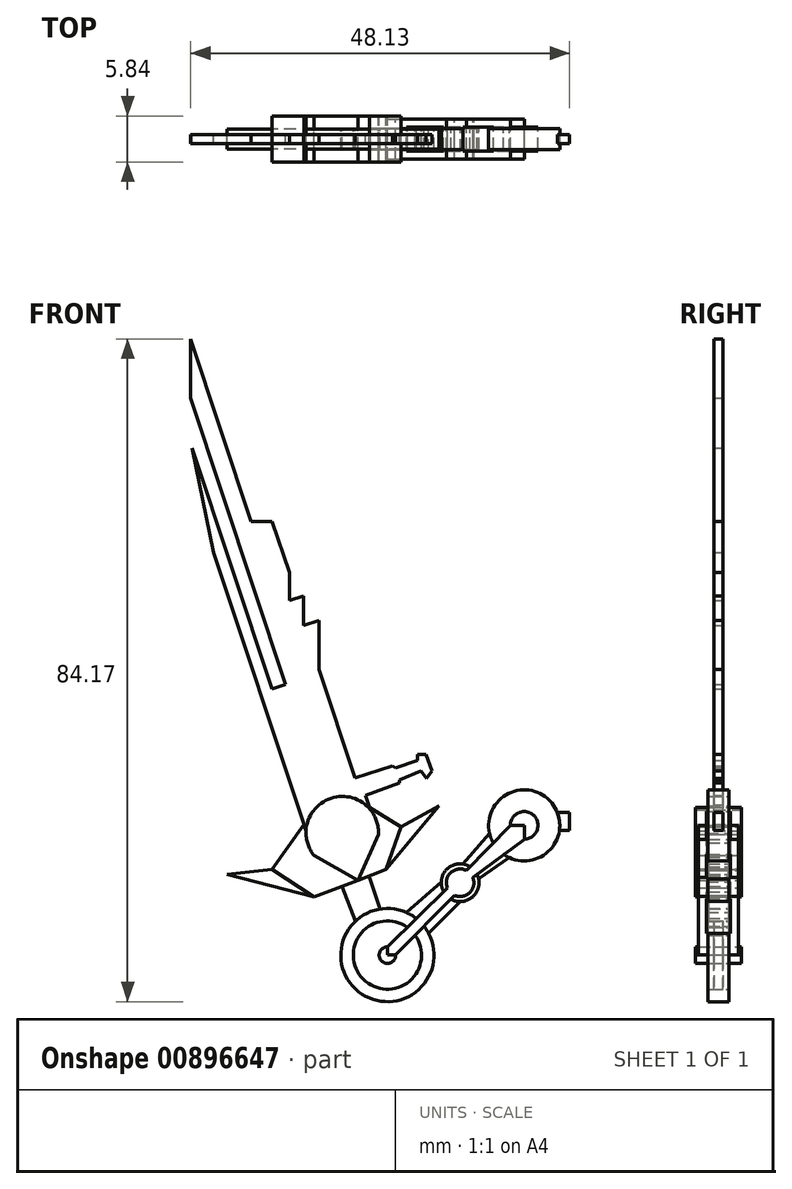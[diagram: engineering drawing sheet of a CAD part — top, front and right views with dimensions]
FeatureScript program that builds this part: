
annotation { "Feature Type Name" : "Feature", "Feature Type Description" : "" }
export const myFeature = defineFeature(function(context is Context, id is Id, definition is map)
    precondition{}
    {
        {
            var Q0;
            Q0=qCreatedBy(makeId("Front.planeOp"),FACE);
            var sketch = newSketch(context, id + "F0", { "sketchPlane" : qUnion([Q0])});
            skLineSegment(sketch, "E0.bottom", {"start": v(-15.76, 7.28) * mm, "end": v(19.82, 7.28) * mm});
            skLineSegment(sketch, "E0.left", {"start": v(-15.76, 7.28) * mm, "end": v(-15.76, 1.57) * mm});
            skLineSegment(sketch, "E0.right", {"start": v(19.82, 7.28) * mm, "end": v(19.82, 1.57) * mm});
            skLineSegment(sketch, "E1", {"start": v(-15.76, 7.28) * mm, "end": v(-19.45, 11.89) * mm});
            skLineSegment(sketch, "E2", {"start": v(23.14, 11.89) * mm, "end": v(19.82, 7.28) * mm});
            skArc(sketch, "E3", {"start": v(23.14, 11.89) * mm, "mid": v(1.84, 40) * mm, "end": v(-19.45, 11.89) * mm});
            skLineSegment(sketch, "E4", {"start": v(-5.9, 38.59) * mm, "end": v(-5.9, 55.58) * mm});
            skLineSegment(sketch, "E5", {"start": v(-5.9, 55.58) * mm, "end": v(-13.15, 34.14) * mm});
            skLineSegment(sketch, "E6", {"start": v(6.13, 39.57) * mm, "end": v(6.13, 56.13) * mm});
            skLineSegment(sketch, "E7", {"start": v(6.13, 56.13) * mm, "end": v(13.75, 36.51) * mm});
            skLineSegment(sketch, "E8", {"start": v(-39.06, 0) * mm, "end": v(-48.21, -3.47) * mm});
            skLineSegment(sketch, "E9", {"start": v(-48.21, -3.47) * mm, "end": v(-53.56, 0) * mm});
            skLineSegment(sketch, "E10", {"start": v(-37.15, 5.44) * mm, "end": v(-39.06, 0) * mm});
            skLineSegment(sketch, "E11", {"start": v(-48.21, 1.77) * mm, "end": v(-60.97, 40.27) * mm});
            skLineSegment(sketch, "E12", {"start": v(-60.97, 40.27) * mm, "end": v(-63.7, 53.56) * mm});
            skLineSegment(sketch, "E13", {"start": v(-63.7, 53.56) * mm, "end": v(-53.56, 22.96) * mm});
            skLineSegment(sketch, "E14", {"start": v(-53.56, 22.96) * mm, "end": v(-51.84, 23.53) * mm});
            skLineSegment(sketch, "E15", {"start": v(-51.84, 23.53) * mm, "end": v(-63.9, 59.88) * mm});
            skLineSegment(sketch, "E16", {"start": v(-63.9, 59.88) * mm, "end": v(-63.9, 67.38) * mm});
            skLineSegment(sketch, "E17", {"start": v(-63.9, 67.38) * mm, "end": v(-57.09, 46.85) * mm});
            skLineSegment(sketch, "E18", {"start": v(-57.09, 46.85) * mm, "end": v(-56.2, 44.2) * mm});
            skLineSegment(sketch, "E19", {"start": v(-56.2, 44.2) * mm, "end": v(-53.56, 44.2) * mm});
            skLineSegment(sketch, "E20", {"start": v(-40.03, 4.48) * mm, "end": v(-41.66, 9.4) * mm});
            skLineSegment(sketch, "E21", {"start": v(-38.25, 13.18) * mm, "end": v(-43.01, 11.6) * mm});
            skLineSegment(sketch, "E22", {"start": v(-43.01, 11.6) * mm, "end": v(-47.6, 25.43) * mm});
            skLineSegment(sketch, "E23", {"start": v(-47.6, 25.43) * mm, "end": v(-47.6, 31.62) * mm});
            skLineSegment(sketch, "E24", {"start": v(-47.6, 31.62) * mm, "end": v(-49.53, 30.98) * mm});
            skLineSegment(sketch, "E25", {"start": v(-49.53, 30.98) * mm, "end": v(-49.53, 34.75) * mm});
            skLineSegment(sketch, "E26", {"start": v(-49.53, 34.75) * mm, "end": v(-51.33, 34.15) * mm});
            skLineSegment(sketch, "E27", {"start": v(-51.33, 34.15) * mm, "end": v(-51.33, 37.7) * mm});
            skLineSegment(sketch, "E28", {"start": v(-51.33, 37.7) * mm, "end": v(-53.56, 44.2) * mm});
            skArc(sketch, "E29", {"start": v(-40.03, 4.48) * mm, "mid": v(-46.08, 9.06) * mm, "end": v(-48.21, 1.77) * mm});
            skLineSegment(sketch, "E30", {"start": v(-42.63, -1.36) * mm, "end": v(-40.03, 4.48) * mm});
            skLineSegment(sketch, "E31", {"start": v(-48.21, 1.77) * mm, "end": v(-42.63, -1.36) * mm});
            skLineSegment(sketch, "E32", {"start": v(-53.56, 0) * mm, "end": v(-49.52, 5.74) * mm});
            skLineSegment(sketch, "E33", {"start": v(-37.15, 5.44) * mm, "end": v(-41.66, 8.2) * mm});
            skArc(sketch, "E34", {"start": v(-10.97, 20.37) * mm, "mid": v(-7.92, 17.42) * mm, "end": v(-5.07, 20.56) * mm});
            skLineSegment(sketch, "E35", {"start": v(-10.97, 20.37) * mm, "end": v(-10.97, 28.85) * mm});
            skLineSegment(sketch, "E36", {"start": v(-5.07, 20.56) * mm, "end": v(-5.07, 28.48) * mm});
            skArc(sketch, "E37", {"start": v(-5.07, 28.48) * mm, "mid": v(-7.82, 31.8) * mm, "end": v(-10.97, 28.85) * mm});
            skArc(sketch, "E38", {"start": v(12.08, 28.85) * mm, "mid": v(9.4, 31.98) * mm, "end": v(6.73, 28.85) * mm});
            skLineSegment(sketch, "E39", {"start": v(6.73, 28.85) * mm, "end": v(6.73, 19.82) * mm});
            skLineSegment(sketch, "E40", {"start": v(12.08, 28.85) * mm, "end": v(12.08, 19.63) * mm});
            skArc(sketch, "E41", {"start": v(6.73, 19.82) * mm, "mid": v(9.31, 17.14) * mm, "end": v(12.08, 19.63) * mm});
            skLineSegment(sketch, "E42", {"start": v(-44.65, -2.12) * mm, "end": v(-42.94, -6.62) * mm});
            skLineSegment(sketch, "E43", {"start": v(-41.24, -0.83) * mm, "end": v(-39.86, -5.04) * mm});
            skCircle(sketch, "E44", {"center": v(-38.9, -10.87) * mm, "radius": 5.92 * mm});
            skCircle(sketch, "E45", {"center": v(-38.9, -10.87) * mm, "radius": 4.33 * mm});
            skCircle(sketch, "E46", {"center": v(-38.9, -10.87) * mm, "radius": 1.05 * mm});
            skFitSpline(sketch, "E47", {"points": [v(-15.76, 7.28) * mm, v(1.84, 17.87) * mm, v(19.82, 7.28) * mm], "startDerivative": vector(35.23, 31.82) * mm, "endDerivative": vector(35.93, -31.74) * mm});
            skCircle(sketch, "E48", {"center": v(-21.52, 5.6) * mm, "radius": 4.51 * mm});
            skLineSegment(sketch, "E49", {"start": v(-15.76, 7.28) * mm, "end": v(-17.33, 7.28) * mm});
            skLineSegment(sketch, "E50", {"start": v(-17.05, 4.97) * mm, "end": v(-15.76, 4.97) * mm});
            skCircle(sketch, "E51", {"center": v(-29.67, -1.68) * mm, "radius": 2.4 * mm});
            skLineSegment(sketch, "E52", {"start": v(-32.06, -1.6) * mm, "end": v(-36.48, -5.47) * mm});
            skLineSegment(sketch, "E53", {"start": v(-29.59, -4.07) * mm, "end": v(-33.65, -8.14) * mm});
            skLineSegment(sketch, "E54", {"start": v(-29.32, 0.7) * mm, "end": v(-25.92, 4.57) * mm});
            skLineSegment(sketch, "E55", {"start": v(-27.31, -1.22) * mm, "end": v(-23.42, 1.5) * mm});
            skCircle(sketch, "E56", {"center": v(-29.67, -1.68) * mm, "radius": 1.75 * mm});
            skCircle(sketch, "E57", {"center": v(-21.52, 5.6) * mm, "radius": 1.75 * mm});
            skLineSegment(sketch, "E58", {"start": v(-21.52, 5.6) * mm, "end": v(-23.27, 5.6) * mm});
            skLineSegment(sketch, "E59", {"start": v(-23.27, 5.6) * mm, "end": v(-28.85, -0.13) * mm});
            skLineSegment(sketch, "E60", {"start": v(-21.52, 5.6) * mm, "end": v(-21.52, 3.85) * mm});
            skLineSegment(sketch, "E61", {"start": v(-21.52, 3.85) * mm, "end": v(-28.06, -1) * mm});
            skLineSegment(sketch, "E62", {"start": v(-38.9, -10.87) * mm, "end": v(-38.9, -9.82) * mm});
            skLineSegment(sketch, "E63", {"start": v(-38.9, -9.82) * mm, "end": v(-31.28, -2.36) * mm});
            skLineSegment(sketch, "E64", {"start": v(-38.9, -10.87) * mm, "end": v(-37.85, -10.87) * mm});
            skLineSegment(sketch, "E65", {"start": v(-37.85, -10.87) * mm, "end": v(-30.38, -3.28) * mm});
            skLineSegment(sketch, "E66", {"start": v(-37.15, 5.44) * mm, "end": v(-32.36, 8.08) * mm});
            skLineSegment(sketch, "E67", {"start": v(-32.36, 8.08) * mm, "end": v(-39.06, 0) * mm});
            skLineSegment(sketch, "E68", {"start": v(-59.26, -0.64) * mm, "end": v(-48.21, -3.47) * mm});
            skLineSegment(sketch, "E69", {"start": v(-53.56, 0) * mm, "end": v(-59.26, -0.64) * mm});
            skLineSegment(sketch, "E70", {"start": v(-38.25, 13.18) * mm, "end": v(-37.87, 12.9) * mm});
            skLineSegment(sketch, "E71", {"start": v(-37.87, 12.9) * mm, "end": v(-35.08, 13.83) * mm});
            skLineSegment(sketch, "E72", {"start": v(-35.08, 13.83) * mm, "end": v(-35.08, 14.65) * mm});
            skLineSegment(sketch, "E73", {"start": v(-35.08, 14.65) * mm, "end": v(-33.97, 14.65) * mm});
            skLineSegment(sketch, "E74", {"start": v(-33.97, 14.65) * mm, "end": v(-33.27, 12.51) * mm});
            skLineSegment(sketch, "E75", {"start": v(-33.27, 12.51) * mm, "end": v(-33.9, 11.6) * mm});
            skLineSegment(sketch, "E76", {"start": v(-33.9, 11.6) * mm, "end": v(-34.63, 12.5) * mm});
            skLineSegment(sketch, "E77", {"start": v(-34.63, 12.5) * mm, "end": v(-37.4, 11.4) * mm});
            skLineSegment(sketch, "E78", {"start": v(-37.4, 11.4) * mm, "end": v(-37.4, 10.98) * mm});
            skLineSegment(sketch, "E79", {"start": v(-37.4, 10.98) * mm, "end": v(-41.66, 9.4) * mm});
            skCircle(sketch, "E80", {"center": v(33.96, -15.69) * mm, "radius": 5 * mm});
            skLineSegment(sketch, "E81", {"start": v(-15.76, 1.57) * mm, "end": v(-5.84, -5.57) * mm});
            skLineSegment(sketch, "E82", {"start": v(-5.84, -5.57) * mm, "end": v(11.89, -5.57) * mm});
            skLineSegment(sketch, "E83", {"start": v(11.89, -5.57) * mm, "end": v(19.82, 1.57) * mm});
            skLineSegment(sketch, "E84", {"start": v(-15.76, 7.28) * mm, "end": v(-5.84, -5.57) * mm});
            skLineSegment(sketch, "E85", {"start": v(19.82, 7.28) * mm, "end": v(11.89, -5.57) * mm});
            skLineSegment(sketch, "E86", {"start": v(25.44, 1.57) * mm, "end": v(25.18, 7.28) * mm});
            skLineSegment(sketch, "E87", {"start": v(-9.91, 12.56) * mm, "end": v(-6, 7.28) * mm});
            skLineSegment(sketch, "E88", {"start": v(13.8, 12.59) * mm, "end": v(9.34, 7.28) * mm});
            skLineSegment(sketch, "E89", {"start": v(25.18, 7.28) * mm, "end": v(30.14, 24.43) * mm});
            skLineSegment(sketch, "E90", {"start": v(30.14, 24.43) * mm, "end": v(32.94, 16.26) * mm});
            skArc(sketch, "E91", {"start": v(32.94, 16.26) * mm, "mid": v(27.23, 9.12) * mm, "end": v(33.8, 2.77) * mm});
            skLineSegment(sketch, "E92", {"start": v(33.8, 2.77) * mm, "end": v(33.8, -2.6) * mm});
            skCircle(sketch, "E93", {"center": v(22.55, 4.35) * mm, "radius": 2.39 * mm});
            skLineSegment(sketch, "E94", {"start": v(24.76, 5.25) * mm, "end": v(25.31, 5.28) * mm});
            skPoint(sketch, "E94.endSnap0", {"position": v(25.31, 4.42) * mm});
            skLineSegment(sketch, "E95", {"start": v(24.9, 3.98) * mm, "end": v(25.33, 4) * mm});
            skLineSegment(sketch, "E96", {"start": v(20.26, 5.03) * mm, "end": v(19.82, 5.03) * mm});
            skLineSegment(sketch, "E97", {"start": v(20.18, 4.02) * mm, "end": v(19.82, 4.02) * mm});
            skLineSegment(sketch, "E98", {"start": v(25.44, 1.57) * mm, "end": v(33.8, -2.6) * mm});
            skCircle(sketch, "E99", {"center": v(34, 9.56) * mm, "radius": 5.31 * mm});
            skLineSegment(sketch, "E100", {"start": v(28.72, 9.03) * mm, "end": v(27.23, 9.03) * mm});
            skLineSegment(sketch, "E101", {"start": v(28.78, 10.5) * mm, "end": v(27.28, 10.5) * mm});
            skArc(sketch, "E102", {"start": v(35.95, 10.39) * mm, "mid": v(34.13, 12.17) * mm, "end": v(32.23, 10.46) * mm});
            skLineSegment(sketch, "E103", {"start": v(32.23, 10.46) * mm, "end": v(32.23, -14.4) * mm});
            skLineSegment(sketch, "E104", {"start": v(32.23, -14.4) * mm, "end": v(33.96, -15.69) * mm});
            skLineSegment(sketch, "E105", {"start": v(33.96, -15.69) * mm, "end": v(35.7, -14.4) * mm});
            skLineSegment(sketch, "E106", {"start": v(35.7, -14.4) * mm, "end": v(35.95, 10.39) * mm});
            skArc(sketch, "E107", {"start": v(32.23, -14.4) * mm, "mid": v(33.96, -18.06) * mm, "end": v(35.7, -14.4) * mm});
            skLineSegment(sketch, "E108", {"start": v(35.2, -20.53) * mm, "end": v(35.2, -28.23) * mm});
            skLineSegment(sketch, "E109", {"start": v(32.87, -20.57) * mm, "end": v(32.87, -28.2) * mm});
            skLineSegment(sketch, "E110", {"start": v(39.5, -25.26) * mm, "end": v(35.95, -41.2) * mm});
            skLineSegment(sketch, "E111", {"start": v(28.5, -25.57) * mm, "end": v(24.97, -22.31) * mm});
            skLineSegment(sketch, "E112", {"start": v(24.97, -22.31) * mm, "end": v(26.4, -28.2) * mm});
            skLineSegment(sketch, "E113", {"start": v(26.4, -28.2) * mm, "end": v(29.95, -31.2) * mm});
            skLineSegment(sketch, "E114", {"start": v(39.5, -25.26) * mm, "end": v(43.36, -22.27) * mm});
            skLineSegment(sketch, "E115", {"start": v(43.36, -22.27) * mm, "end": v(41.75, -28.56) * mm});
            skLineSegment(sketch, "E116", {"start": v(41.75, -28.56) * mm, "end": v(38.35, -30.4) * mm});
            skLineSegment(sketch, "E117", {"start": v(28.5, -35.98) * mm, "end": v(32.54, -41.2) * mm});
            skLineSegment(sketch, "E118", {"start": v(39.54, -35.66) * mm, "end": v(35.95, -41.2) * mm});
            skCircle(sketch, "E119", {"center": v(34.07, -31.3) * mm, "radius": 2.67 * mm});
            skLineSegment(sketch, "E120", {"start": v(28.5, -25.57) * mm, "end": v(34.09, -22.67) * mm});
            skLineSegment(sketch, "E121", {"start": v(34.09, -22.67) * mm, "end": v(39.5, -25.26) * mm});
            skLineSegment(sketch, "E122", {"start": v(32.87, -28.2) * mm, "end": v(34.07, -31.3) * mm});
            skLineSegment(sketch, "E123", {"start": v(34.07, -31.3) * mm, "end": v(35.2, -28.23) * mm});
            skArc(sketch, "E124", {"start": v(33.68, -30.28) * mm, "mid": v(34.02, -32.42) * mm, "end": v(34.44, -30.3) * mm});
            skLineSegment(sketch, "E125", {"start": v(35.2, -28.23) * mm, "end": v(38.35, -30.4) * mm});
            skLineSegment(sketch, "E126", {"start": v(32.87, -28.2) * mm, "end": v(29.95, -31.2) * mm});
            skLineSegment(sketch, "E127", {"start": v(29.95, -31.2) * mm, "end": v(28.5, -35.98) * mm});
            skLineSegment(sketch, "E128", {"start": v(38.35, -30.4) * mm, "end": v(39.54, -35.66) * mm});
            skLineSegment(sketch, "E129", {"start": v(28.5, -25.57) * mm, "end": v(29.95, -31.2) * mm});
            skLineSegment(sketch, "E130", {"start": v(29.95, -31.2) * mm, "end": v(32.54, -41.2) * mm});
            skLineSegment(sketch, "E131", {"start": v(32.54, -41.2) * mm, "end": v(32.54, -41.85) * mm});
            skLineSegment(sketch, "E132", {"start": v(32.54, -41.85) * mm, "end": v(35.95, -41.85) * mm});
            skLineSegment(sketch, "E133", {"start": v(35.95, -41.85) * mm, "end": v(35.95, -41.2) * mm});
            skLineSegment(sketch, "E134", {"start": v(34.02, -37.9) * mm, "end": v(32.54, -41.2) * mm});
            skLineSegment(sketch, "E135", {"start": v(34.02, -37.9) * mm, "end": v(35.95, -41.2) * mm});
            skCircle(sketch, "E136", {"center": v(34.18, -43.8) * mm, "radius": 1.74 * mm});
            skLineSegment(sketch, "E137", {"start": v(32.86, -41.85) * mm, "end": v(32.86, -42.67) * mm});
            skLineSegment(sketch, "E138", {"start": v(33.2, -41.85) * mm, "end": v(33.2, -42.37) * mm});
            skLineSegment(sketch, "E139", {"start": v(33.93, -41.85) * mm, "end": v(33.93, -42.08) * mm});
            skLineSegment(sketch, "E140", {"start": v(34.32, -41.85) * mm, "end": v(34.32, -42.06) * mm});
            skLineSegment(sketch, "E141", {"start": v(35.06, -41.85) * mm, "end": v(35.06, -42.3) * mm});
            skLineSegment(sketch, "E142", {"start": v(35.42, -41.85) * mm, "end": v(35.42, -42.57) * mm});
            skLineSegment(sketch, "E143", {"start": v(31.7, -43.74) * mm, "end": v(31.7, -46.07) * mm});
            skLineSegment(sketch, "E144", {"start": v(31.7, -46.07) * mm, "end": v(36.58, -46.07) * mm});
            skLineSegment(sketch, "E145", {"start": v(36.58, -46.07) * mm, "end": v(36.58, -43.76) * mm});
            skLineSegment(sketch, "E146", {"start": v(33.9, -45.52) * mm, "end": v(33.9, -45.7) * mm});
            skLineSegment(sketch, "E147", {"start": v(34.48, -45.51) * mm, "end": v(34.48, -45.7) * mm});
            skLineSegment(sketch, "E148", {"start": v(31.7, -43.74) * mm, "end": v(32.14, -43.74) * mm});
            skLineSegment(sketch, "E149", {"start": v(36.58, -43.76) * mm, "end": v(36.19, -43.76) * mm});
            skLineSegment(sketch, "E150", {"start": v(32.47, -44.07) * mm, "end": v(32.14, -44.07) * mm});
            skLineSegment(sketch, "E151", {"start": v(32.54, -44.37) * mm, "end": v(32.14, -44.37) * mm});
            skLineSegment(sketch, "E152", {"start": v(35.91, -44) * mm, "end": v(36.2, -44) * mm});
            skLineSegment(sketch, "E153", {"start": v(32.14, -43.74) * mm, "end": v(32.14, -44.07) * mm});
            skArc(sketch, "E154", {"start": v(32.14, -44.37) * mm, "mid": v(32.8, -45.34) * mm, "end": v(33.9, -45.7) * mm});
            skLineSegment(sketch, "E155", {"start": v(35.86, -44.27) * mm, "end": v(36.2, -44.27) * mm});
            skLineSegment(sketch, "E156", {"start": v(36.19, -43.76) * mm, "end": v(36.2, -44) * mm});
            skArc(sketch, "E157", {"start": v(34.48, -45.7) * mm, "mid": v(35.58, -45.28) * mm, "end": v(36.2, -44.27) * mm});
            skLineSegment(sketch, "E158.4", {"start": v(32.84, -46.15) * mm, "end": v(35.8, -46.16) * mm});
            skLineSegment(sketch, "E159", {"start": v(32.95, -46.07) * mm, "end": v(32.95, -46.15) * mm});
            skLineSegment(sketch, "E160", {"start": v(33.2, -46.07) * mm, "end": v(33.2, -46.15) * mm});
            skLineSegment(sketch, "E161", {"start": v(33.55, -46.07) * mm, "end": v(33.55, -46.15) * mm});
            skLineSegment(sketch, "E162", {"start": v(33.86, -46.07) * mm, "end": v(33.86, -46.15) * mm});
            skLineSegment(sketch, "E163", {"start": v(34.1, -46.07) * mm, "end": v(34.1, -46.15) * mm});
            skLineSegment(sketch, "E164", {"start": v(34.36, -46.07) * mm, "end": v(34.36, -46.16) * mm});
            skLineSegment(sketch, "E165", {"start": v(34.65, -46.07) * mm, "end": v(34.65, -46.16) * mm});
            skLineSegment(sketch, "E166", {"start": v(34.92, -46.07) * mm, "end": v(34.92, -46.16) * mm});
            skLineSegment(sketch, "E167", {"start": v(35.18, -46.07) * mm, "end": v(35.18, -46.16) * mm});
            skLineSegment(sketch, "E168", {"start": v(35.46, -46.07) * mm, "end": v(35.46, -46.16) * mm});
            skLineSegment(sketch, "E169", {"start": v(35.62, -46.07) * mm, "end": v(35.62, -46.16) * mm});
            skLineSegment(sketch, "E170.0", {"start": v(38.42, -49.81) * mm, "end": v(36.32, -53.4) * mm});
            skLineSegment(sketch, "E170.1", {"start": v(36.32, -53.4) * mm, "end": v(32.17, -53.36) * mm});
            skLineSegment(sketch, "E170.2", {"start": v(32.17, -53.36) * mm, "end": v(30.12, -49.75) * mm});
            skLineSegment(sketch, "E170.3", {"start": v(30.12, -49.75) * mm, "end": v(32.22, -46.17) * mm});
            skLineSegment(sketch, "E170.4", {"start": v(32.22, -46.17) * mm, "end": v(36.37, -46.2) * mm});
            skLineSegment(sketch, "E170.5", {"start": v(36.37, -46.2) * mm, "end": v(38.42, -49.81) * mm});
            skPoint(sketch, "E170.0.midPoint", {"position": v(37.37, -51.6) * mm});
            skArc(sketch, "E171", {"start": v(30.12, -49.75) * mm, "mid": v(34.23, -54.9) * mm, "end": v(38.42, -49.81) * mm});
            skLineSegment(sketch, "E172", {"start": v(30.12, -49.75) * mm, "end": v(34.26, -50.65) * mm});
            skLineSegment(sketch, "E173", {"start": v(38.42, -49.81) * mm, "end": v(34.26, -50.65) * mm});
            skLineSegment(sketch, "E174", {"start": v(30.04, -51.06) * mm, "end": v(28.9, -51.7) * mm});
            skLineSegment(sketch, "E175", {"start": v(28.9, -51.7) * mm, "end": v(30.27, -52.09) * mm});
            skLineSegment(sketch, "E176", {"start": v(38.48, -51.12) * mm, "end": v(39.68, -51.78) * mm});
            skLineSegment(sketch, "E177", {"start": v(39.68, -51.78) * mm, "end": v(38.2, -52.22) * mm});
            skLineSegment(sketch, "E178", {"start": v(31.2, -53.6) * mm, "end": v(30.81, -54.98) * mm});
            skLineSegment(sketch, "E179", {"start": v(30.81, -54.98) * mm, "end": v(32.15, -54.33) * mm});
            skLineSegment(sketch, "E180", {"start": v(33.68, -54.85) * mm, "end": v(34.23, -56.04) * mm});
            skPoint(sketch, "E180.endSnap0", {"position": v(34.23, -54.9) * mm});
            skLineSegment(sketch, "E181", {"start": v(34.23, -56.04) * mm, "end": v(34.95, -54.84) * mm});
            skLineSegment(sketch, "E182", {"start": v(36.34, -54.35) * mm, "end": v(37.7, -55.15) * mm});
            skPoint(sketch, "E182.startSnap0", {"position": v(36.34, -50.23) * mm});
            skLineSegment(sketch, "E183", {"start": v(37.7, -55.15) * mm, "end": v(37.38, -53.53) * mm});
            skLineSegment(sketch, "E184.top", {"start": v(-5.84, -33.89) * mm, "end": v(12.35, -33.89) * mm});
            skLineSegment(sketch, "E184.left", {"start": v(-5.84, -30.08) * mm, "end": v(-5.84, -33.89) * mm});
            skLineSegment(sketch, "E184.right", {"start": v(12.35, -30.08) * mm, "end": v(12.35, -33.89) * mm});
            skLineSegment(sketch, "E185", {"start": v(-5.84, -30.08) * mm, "end": v(-11.43, -30.08) * mm});
            skLineSegment(sketch, "E186", {"start": v(-11.43, -30.08) * mm, "end": v(-5.84, -33.89) * mm});
            skLineSegment(sketch, "E187", {"start": v(12.35, -30.08) * mm, "end": v(18.1, -30.08) * mm});
            skLineSegment(sketch, "E188", {"start": v(18.1, -30.08) * mm, "end": v(12.35, -33.89) * mm});
            skCircle(sketch, "E189", {"center": v(3.02, -18.97) * mm, "radius": 6.33 * mm});
            skPoint(sketch, "E189.centerSnap0", {"position": v(3.02, -5.57) * mm});
            skLineSegment(sketch, "E190", {"start": v(-5.84, -5.57) * mm, "end": v(3.02, -18.97) * mm});
            skLineSegment(sketch, "E191", {"start": v(11.89, -5.57) * mm, "end": v(3.02, -18.97) * mm});
            skLineSegment(sketch, "E192", {"start": v(3.02, -18.97) * mm, "end": v(-5.84, -30.08) * mm});
            skLineSegment(sketch, "E193", {"start": v(3.02, -18.97) * mm, "end": v(12.35, -30.08) * mm});
            skPoint(sketch, "E194", {"position": v(-0.47, -13.7) * mm});
            skPoint(sketch, "E195", {"position": v(6.51, -13.7) * mm});
            skPoint(sketch, "E196", {"position": v(-0.93, -23.92) * mm});
            skPoint(sketch, "E197", {"position": v(7.1, -23.82) * mm});
            skPoint(sketch, "E198", {"position": v(3.25, -42.98) * mm});
            skArc(sketch, "E199", {"start": v(-5.84, -33.89) * mm, "mid": v(3.25, -42.98) * mm, "end": v(12.35, -33.89) * mm});
            skLineSegment(sketch, "E200", {"start": v(-9.7, -37.42) * mm, "end": v(-14.57, -53.8) * mm});
            skLineSegment(sketch, "E201", {"start": v(-14.57, -53.8) * mm, "end": v(-8.4, -55.63) * mm});
            skLineSegment(sketch, "E202", {"start": v(-8.4, -55.63) * mm, "end": v(0, -46) * mm});
            skArc(sketch, "E203", {"start": v(-9.7, -37.42) * mm, "mid": v(-6.49, -43.56) * mm, "end": v(0, -46) * mm});
            skCircle(sketch, "E204", {"center": v(-5.02, -41.77) * mm, "radius": 2.38 * mm});
            skCircle(sketch, "E205", {"center": v(3.34, -31.78) * mm, "radius": 2.83 * mm});
            skArc(sketch, "E206", {"start": v(5.13, -33.39) * mm, "mid": v(3.43, -31.79) * mm, "end": v(1.57, -33.2) * mm});
            skArc(sketch, "E207", {"start": v(5.13, -33.39) * mm, "mid": v(3.38, -32.7) * mm, "end": v(1.57, -33.2) * mm});
            skCircle(sketch, "E208", {"center": v(-13.17, -57.63) * mm, "radius": 2.28 * mm});
            skLineSegment(sketch, "E209", {"start": v(-17.2, -56) * mm, "end": v(-17.2, -71.94) * mm});
            skLineSegment(sketch, "E210", {"start": v(-8.84, -57.78) * mm, "end": v(-10.78, -72.54) * mm});
            skLineSegment(sketch, "E211", {"start": v(-17.2, -56) * mm, "end": v(-15.52, -60.13) * mm});
            skLineSegment(sketch, "E212", {"start": v(-15.52, -60.13) * mm, "end": v(-11.73, -60.9) * mm});
            skLineSegment(sketch, "E213", {"start": v(-11.73, -60.9) * mm, "end": v(-8.84, -57.78) * mm});
            skLineSegment(sketch, "E214", {"start": v(-13.32, -54.16) * mm, "end": v(-14.07, -55.54) * mm});
            skLineSegment(sketch, "E215", {"start": v(-13.12, -54.22) * mm, "end": v(-13.6, -55.39) * mm});
            skLineSegment(sketch, "E216", {"start": v(-11.96, -54.57) * mm, "end": v(-12.54, -55.44) * mm});
            skLineSegment(sketch, "E217", {"start": v(-11.42, -54.73) * mm, "end": v(-12.02, -55.66) * mm});
            skLineSegment(sketch, "E218", {"start": v(-10.6, -54.98) * mm, "end": v(-11.49, -56.09) * mm});
            skLineSegment(sketch, "E219", {"start": v(-10.3, -55.06) * mm, "end": v(-11.21, -56.46) * mm});
            skCircle(sketch, "E220", {"center": v(-13.17, -57.63) * mm, "radius": 0.68 * mm});
            skCircle(sketch, "E221", {"center": v(-14.33, -75.96) * mm, "radius": 3.36 * mm});
            skLineSegment(sketch, "E222", {"start": v(-17.2, -71.94) * mm, "end": v(-18.76, -73.06) * mm});
            skLineSegment(sketch, "E223", {"start": v(-18.76, -73.06) * mm, "end": v(-15.3, -71.94) * mm});
            skLineSegment(sketch, "E224", {"start": v(-15.3, -71.94) * mm, "end": v(-12.92, -71.94) * mm});
            skLineSegment(sketch, "E225", {"start": v(-12.92, -71.94) * mm, "end": v(-10.07, -73.28) * mm});
            skLineSegment(sketch, "E226", {"start": v(-10.07, -73.28) * mm, "end": v(-10.78, -72.54) * mm});
            skLineSegment(sketch, "E227", {"start": v(-17.2, -71.94) * mm, "end": v(-15.52, -60.13) * mm});
            skLineSegment(sketch, "E228", {"start": v(-11.73, -60.9) * mm, "end": v(-10.78, -72.54) * mm});
            skLineSegment(sketch, "E229", {"start": v(-15.3, -71.94) * mm, "end": v(-15.23, -72.72) * mm});
            skLineSegment(sketch, "E230", {"start": v(-14.98, -71.94) * mm, "end": v(-14.98, -72.65) * mm});
            skLineSegment(sketch, "E231", {"start": v(-14.41, -71.94) * mm, "end": v(-14.41, -72.6) * mm});
            skLineSegment(sketch, "E232", {"start": v(-14.1, -71.94) * mm, "end": v(-14.1, -72.6) * mm});
            skLineSegment(sketch, "E233", {"start": v(-12.92, -71.94) * mm, "end": v(-13.14, -72.81) * mm});
            skLineSegment(sketch, "E234", {"start": v(-13.36, -71.94) * mm, "end": v(-13.36, -72.74) * mm});
            skLineSegment(sketch, "E235", {"start": v(-17.7, -80.72) * mm, "end": v(-14.88, -80.72) * mm});
            skLineSegment(sketch, "E236", {"start": v(-14.88, -80.72) * mm, "end": v(-14.2, -79.32) * mm});
            skLineSegment(sketch, "E237", {"start": v(-14.2, -79.32) * mm, "end": v(-13.75, -80.68) * mm});
            skLineSegment(sketch, "E238", {"start": v(-13.75, -80.68) * mm, "end": v(-11.02, -80.68) * mm});
            skLineSegment(sketch, "E239", {"start": v(-15.18, -58.7) * mm, "end": v(-15.52, -60.13) * mm});
            skLineSegment(sketch, "E240", {"start": v(-14.7, -59.32) * mm, "end": v(-15.15, -60.2) * mm});
            skLineSegment(sketch, "E241", {"start": v(-13.95, -59.78) * mm, "end": v(-13.95, -60.45) * mm});
            skLineSegment(sketch, "E242", {"start": v(-13.3, -59.9) * mm, "end": v(-13.62, -60.51) * mm});
            skLineSegment(sketch, "E243", {"start": v(-12.48, -59.8) * mm, "end": v(-12.66, -60.7) * mm});
            skLineSegment(sketch, "E244", {"start": v(-11.9, -59.53) * mm, "end": v(-12.17, -60.8) * mm});
            skLineSegment(sketch, "E245", {"start": v(-17.7, -76.16) * mm, "end": v(-20.3, -80.77) * mm});
            skLineSegment(sketch, "E246", {"start": v(-20.3, -80.77) * mm, "end": v(-17.7, -80.72) * mm});
            skLineSegment(sketch, "E247", {"start": v(-11.02, -80.68) * mm, "end": v(-7.93, -80.72) * mm});
            skLineSegment(sketch, "E248", {"start": v(-7.93, -80.72) * mm, "end": v(-10.97, -76) * mm});
            skLineSegment(sketch, "E249", {"start": v(1.57, -30.46) * mm, "end": v(2.07, -30.8) * mm});
            skLineSegment(sketch, "E250", {"start": v(2.07, -30.8) * mm, "end": v(1.6, -31.48) * mm});
            skLineSegment(sketch, "E251", {"start": v(1.6, -31.48) * mm, "end": v(1.99, -31.75) * mm});
            skLineSegment(sketch, "E252", {"start": v(1.99, -31.75) * mm, "end": v(2.48, -31.04) * mm});
            skLineSegment(sketch, "E253", {"start": v(2.48, -31.04) * mm, "end": v(3.18, -31.53) * mm});
            skLineSegment(sketch, "E254", {"start": v(3.18, -31.53) * mm, "end": v(3.4, -31.21) * mm});
            skLineSegment(sketch, "E255", {"start": v(3.4, -31.21) * mm, "end": v(2.73, -30.74) * mm});
            skLineSegment(sketch, "E256", {"start": v(2.73, -30.74) * mm, "end": v(3.1, -30.2) * mm});
            skLineSegment(sketch, "E257", {"start": v(3.1, -30.2) * mm, "end": v(2.67, -29.9) * mm});
            skLineSegment(sketch, "E258", {"start": v(2.67, -29.9) * mm, "end": v(2.29, -30.45) * mm});
            skLineSegment(sketch, "E259", {"start": v(2.29, -30.45) * mm, "end": v(1.82, -30.13) * mm});
            skLineSegment(sketch, "E260", {"start": v(1.82, -30.13) * mm, "end": v(1.57, -30.46) * mm});
            skLineSegment(sketch, "E261", {"start": v(3.5, -30.25) * mm, "end": v(3.92, -29.83) * mm});
            skLineSegment(sketch, "E262", {"start": v(3.92, -29.83) * mm, "end": v(4.51, -30.43) * mm});
            skLineSegment(sketch, "E263", {"start": v(4.51, -30.43) * mm, "end": v(5.1, -29.85) * mm});
            skLineSegment(sketch, "E264", {"start": v(5.1, -29.85) * mm, "end": v(5.47, -30.23) * mm});
            skLineSegment(sketch, "E265", {"start": v(5.47, -30.23) * mm, "end": v(4.88, -30.82) * mm});
            skLineSegment(sketch, "E266", {"start": v(4.88, -30.82) * mm, "end": v(5.51, -31.45) * mm});
            skLineSegment(sketch, "E267", {"start": v(5.51, -31.45) * mm, "end": v(5.08, -31.87) * mm});
            skLineSegment(sketch, "E268", {"start": v(5.08, -31.87) * mm, "end": v(4.43, -31.22) * mm});
            skLineSegment(sketch, "E269", {"start": v(4.43, -31.22) * mm, "end": v(3.93, -31.71) * mm});
            skLineSegment(sketch, "E270", {"start": v(3.93, -31.71) * mm, "end": v(3.59, -31.26) * mm});
            skLineSegment(sketch, "E271", {"start": v(3.59, -31.26) * mm, "end": v(4.04, -30.8) * mm});
            skLineSegment(sketch, "E272", {"start": v(4.04, -30.8) * mm, "end": v(3.5, -30.25) * mm});
            skLineSegment(sketch, "E273", {"start": v(-5.84, -30.08) * mm, "end": v(1.07, -30.08) * mm});
            skLineSegment(sketch, "E274", {"start": v(12.35, -30.08) * mm, "end": v(5.6, -30.08) * mm});
            skLineSegment(sketch, "E275.MirrorCS", {"start": v(21.09, -71.84) * mm, "end": v(21.1, -72.5) * mm});
            skLineSegment(sketch, "E276.MirrorCS", {"start": v(19.08, -59.72) * mm, "end": v(19.27, -60.62) * mm});
            skLineSegment(sketch, "E277.MirrorCS", {"start": v(21.97, -71.84) * mm, "end": v(21.9, -72.6) * mm});
            skLineSegment(sketch, "E278.MirrorCS", {"start": v(21.78, -58.6) * mm, "end": v(22.12, -60.02) * mm});
            skLineSegment(sketch, "E279.MirrorCS", {"start": v(21.3, -59.22) * mm, "end": v(21.75, -60.1) * mm});
            skLineSegment(sketch, "E280.MirrorCS", {"start": v(20.78, -71.84) * mm, "end": v(20.78, -72.5) * mm});
            skLineSegment(sketch, "E281.MirrorCS", {"start": v(20.04, -71.85) * mm, "end": v(20.04, -72.64) * mm});
            skLineSegment(sketch, "E282.MirrorCS", {"start": v(18.5, -59.45) * mm, "end": v(18.77, -60.72) * mm});
            skLineSegment(sketch, "E283.MirrorCS", {"start": v(21.97, -71.84) * mm, "end": v(19.6, -71.85) * mm});
            skLineSegment(sketch, "E284.MirrorCS", {"start": v(21.65, -71.84) * mm, "end": v(21.65, -72.55) * mm});
            skLineSegment(sketch, "E285.MirrorCS", {"start": v(19.6, -71.85) * mm, "end": v(16.75, -73.2) * mm});
            skLineSegment(sketch, "E286.MirrorCS", {"start": v(19.6, -71.85) * mm, "end": v(19.82, -72.72) * mm});
            skLineSegment(sketch, "E287.MirrorCS", {"start": v(22.12, -60.02) * mm, "end": v(18.34, -60.81) * mm});
            skLineSegment(sketch, "E288.MirrorCS", {"start": v(25.44, -72.93) * mm, "end": v(21.97, -71.84) * mm});
            skLineSegment(sketch, "E289.MirrorCS", {"start": v(16.75, -73.2) * mm, "end": v(17.46, -72.46) * mm});
            skLineSegment(sketch, "E290.MirrorCS", {"start": v(19.9, -59.81) * mm, "end": v(20.23, -60.42) * mm});
            skLineSegment(sketch, "E291.MirrorCS", {"start": v(20.55, -59.68) * mm, "end": v(20.56, -60.35) * mm});
            skLineSegment(sketch, "E292.MirrorCS", {"start": v(23.87, -71.82) * mm, "end": v(25.44, -72.93) * mm});
            skCircle(sketch, "E293.MirrorC", {"center": v(19.76, -57.54) * mm, "radius": 0.68 * mm});
            skLineSegment(sketch, "E294.MirrorCS", {"start": v(19.7, -54.13) * mm, "end": v(20.17, -55.3) * mm});
            skLineSegment(sketch, "E295.MirrorCS", {"start": v(19.89, -54.07) * mm, "end": v(20.65, -55.44) * mm});
            skLineSegment(sketch, "E296.MirrorCS", {"start": v(24.42, -80.6) * mm, "end": v(21.6, -80.61) * mm});
            skLineSegment(sketch, "E297.MirrorCS", {"start": v(18, -54.64) * mm, "end": v(18.6, -55.57) * mm});
            skLineSegment(sketch, "E298.MirrorCS", {"start": v(20.93, -79.22) * mm, "end": v(20.47, -80.58) * mm});
            skLineSegment(sketch, "E299.MirrorCS", {"start": v(17.74, -80.6) * mm, "end": v(14.65, -80.65) * mm});
            skLineSegment(sketch, "E300.MirrorCS", {"start": v(17.17, -54.9) * mm, "end": v(18.07, -56) * mm});
            skLineSegment(sketch, "E301.MirrorCS", {"start": v(21.13, -53.69) * mm, "end": v(14.97, -55.56) * mm});
            skLineSegment(sketch, "E302.MirrorCS", {"start": v(16.88, -54.98) * mm, "end": v(17.8, -56.37) * mm});
            skLineSegment(sketch, "E303.MirrorCS", {"start": v(21.6, -80.61) * mm, "end": v(20.93, -79.22) * mm});
            skLineSegment(sketch, "E304.MirrorCS", {"start": v(20.47, -80.58) * mm, "end": v(17.74, -80.6) * mm});
            skLineSegment(sketch, "E305.MirrorCS", {"start": v(18.53, -54.48) * mm, "end": v(19.12, -55.35) * mm});
            skLineSegment(sketch, "E306.MirrorCS", {"start": v(27.02, -80.63) * mm, "end": v(24.42, -80.6) * mm});
            skCircle(sketch, "E307.MirrorC", {"center": v(19.76, -57.54) * mm, "radius": 2.28 * mm});
            skLineSegment(sketch, "E308.MirrorCS", {"start": v(23.77, -55.87) * mm, "end": v(22.12, -60.02) * mm});
            skLineSegment(sketch, "E309.MirrorCS", {"start": v(14.97, -55.56) * mm, "end": v(6.52, -45.98) * mm});
            skLineSegment(sketch, "E310.MirrorCS", {"start": v(18.34, -60.81) * mm, "end": v(15.44, -57.71) * mm});
            skLineSegment(sketch, "E311.MirrorCS", {"start": v(23.87, -71.82) * mm, "end": v(22.12, -60.02) * mm});
            skCircle(sketch, "E312.MirrorC", {"center": v(21.03, -75.85) * mm, "radius": 3.36 * mm});
            skLineSegment(sketch, "E313.MirrorCS", {"start": v(16.17, -37.35) * mm, "end": v(21.13, -53.69) * mm});
            skArc(sketch, "E314.MirrorCS", {"start": v(16.17, -37.35) * mm, "mid": v(13, -43.5) * mm, "end": v(6.52, -45.98) * mm});
            skLineSegment(sketch, "E315.MirrorCS", {"start": v(14.65, -80.65) * mm, "end": v(17.67, -75.91) * mm});
            skLineSegment(sketch, "E316.MirrorCS", {"start": v(24.39, -76.04) * mm, "end": v(27.02, -80.63) * mm});
            skLineSegment(sketch, "E317.MirrorCS", {"start": v(15.44, -57.71) * mm, "end": v(17.46, -72.46) * mm});
            skLineSegment(sketch, "E318.MirrorCS", {"start": v(23.77, -55.87) * mm, "end": v(23.87, -71.82) * mm});
            skLineSegment(sketch, "E319.MirrorCS", {"start": v(18.34, -60.81) * mm, "end": v(17.46, -72.46) * mm});
            skCircle(sketch, "E320.MirrorC", {"center": v(11.52, -41.73) * mm, "radius": 2.38 * mm});
            skSolve(sketch);
        }
        {
            var Q0;
            {var subQ0=sQuery(id+"F0.wireOp",EDGE,"E29");var subQ1=sQuery(id+"F0.wireOp",EDGE,"E11");var subQ3=makeQuery(id+"F0.imprint","INTERSECT",VERTEX,{"derivedFrom":[subQ1,subQ0]});Q0=makeQuery(id+"F0.imprint","IMPRINT",FACE,{"disambiguationData":[TD([[makeQuery(id+"F0.imprint","IMPRINT",EDGE,{"disambiguationData":[TD([[subQ3,1.0]])],"derivedFrom":subQ1}),1.0]])]});}
            var Q1;
            {var subQ6=sQuery(id+"F0.wireOp",EDGE,"E30");Q1=makeQuery(id+"F0.imprint","IMPRINT",FACE,{"disambiguationData":[TD([[makeQuery(id+"F0.imprint","IMPRINT",EDGE,{"derivedFrom":subQ6}),1.0]])]});}
            var Q2;
            {var subQ0=sQuery(id+"F0.wireOp",EDGE,"E29");var subQ1=sQuery(id+"F0.wireOp",EDGE,"E20");var subQ3=makeQuery(id+"F0.imprint","INTERSECT",VERTEX,{"derivedFrom":[subQ1,subQ0]});Q2=makeQuery(id+"F0.imprint","IMPRINT",FACE,{"disambiguationData":[TD([[makeQuery(id+"F0.imprint","IMPRINT",EDGE,{"disambiguationData":[TD([[subQ3,1.0]])],"derivedFrom":subQ1}),-1.0]])]});}
            var Q3;
            Q3=makeQuery(id+"F0.imprint","IMPRINT",FACE,{"disambiguationData":[TD([[makeQuery(id+"F0.imprint","IMPRINT",EDGE,{"derivedFrom":sQuery(id+"F0.wireOp",EDGE,"E10")}),1.0]])]});
            var Q4;
            Q4=makeQuery(id+"F0.imprint","IMPRINT",FACE,{"disambiguationData":[TD([[makeQuery(id+"F0.imprint","IMPRINT",EDGE,{"derivedFrom":sQuery(id+"F0.wireOp",EDGE,"E9")}),1.0]])]});
            var Q5;
            {var subQ0=sQuery(id+"F0.wireOp",EDGE,"E42");var subQ1=sQuery(id+"F0.wireOp",EDGE,"E8");var subQ2=makeQuery(id+"F0.imprint","INTERSECT",VERTEX,{"derivedFrom":[subQ1,subQ0]});Q5=makeQuery(id+"F0.imprint","IMPRINT",FACE,{"disambiguationData":[TD([[makeQuery(id+"F0.imprint","IMPRINT",EDGE,{"disambiguationData":[TD([[subQ2,-1.0]])],"derivedFrom":subQ0}),1.0]])]});}
            extrude(context, id + "F1", {"entities" : qUnion([Q0, Q1, Q2, Q3, Q4, Q5]), "endBound" : BoundingType.SYMMETRIC, "depth" : 2.54 * mm, "offsetDistance" : 25.4 * mm});
        }
        {
            var Q0;
            {var subQ0=sQuery(id+"F0.wireOp",EDGE,"E48");var subQ11=makeQuery(id+"F0.imprint","INTERSECT",VERTEX,{"derivedFrom":[subQ0,sQuery(id+"F0.wireOp",EDGE,"E49")]});Q0=makeQuery(id+"F0.imprint","IMPRINT",FACE,{"disambiguationData":[TD([[makeQuery(id+"F0.imprint","IMPRINT",EDGE,{"disambiguationData":[TD([[subQ11,-1.0]])],"derivedFrom":subQ0}),1.0]])]});}
            var Q1;
            {var subQ0=sQuery(id+"F0.wireOp",EDGE,"E44");var subQ6=makeQuery(id+"F0.imprint","INTERSECT",VERTEX,{"derivedFrom":[subQ0,sQuery(id+"F0.wireOp",EDGE,"E53")]});Q1=makeQuery(id+"F0.imprint","IMPRINT",FACE,{"disambiguationData":[TD([[makeQuery(id+"F0.imprint","IMPRINT",EDGE,{"disambiguationData":[TD([[subQ6,-1.0]])],"derivedFrom":subQ0}),1.0]])]});}
            var Q2;
            {var subQ0=sQuery(id+"F0.wireOp",EDGE,"E51");var subQ2=makeQuery(id+"F0.imprint","INTERSECT",VERTEX,{"derivedFrom":[subQ0,sQuery(id+"F0.wireOp",EDGE,"E55")]});Q2=makeQuery(id+"F0.imprint","IMPRINT",FACE,{"disambiguationData":[TD([[makeQuery(id+"F0.imprint","IMPRINT",EDGE,{"disambiguationData":[TD([[subQ2,-1.0]])],"derivedFrom":subQ0}),1.0]])]});}
            var Q3;
            {var subQ0=sQuery(id+"F0.wireOp",EDGE,"E51");var subQ8=makeQuery(id+"F0.imprint","INTERSECT",VERTEX,{"derivedFrom":[subQ0,sQuery(id+"F0.wireOp",EDGE,"E54")]});Q3=makeQuery(id+"F0.imprint","IMPRINT",FACE,{"disambiguationData":[TD([[makeQuery(id+"F0.imprint","IMPRINT",EDGE,{"disambiguationData":[TD([[subQ8,1.0]])],"derivedFrom":subQ0}),1.0]])]});}
            extrude(context, id + "F2", {"entities" : qUnion([Q0, Q1, Q2, Q3]), "operationType" : NewBodyOperationType.ADD, "endBound" : BoundingType.SYMMETRIC, "depth" : 2.7 * mm, "offsetDistance" : 25.4 * mm});
        }
        {
            var Q0;
            {var subQ0=sQuery(id+"F0.wireOp",EDGE,"E58");Q0=makeQuery(id+"F0.imprint","IMPRINT",FACE,{"disambiguationData":[TD([[makeQuery(id+"F0.imprint","IMPRINT",EDGE,{"derivedFrom":subQ0}),-1.0]])]});}
            var Q1;
            {var subQ0=sQuery(id+"F0.wireOp",EDGE,"E54");Q1=makeQuery(id+"F0.imprint","IMPRINT",FACE,{"disambiguationData":[TD([[makeQuery(id+"F0.imprint","IMPRINT",EDGE,{"derivedFrom":subQ0}),-1.0]])]});}
            var Q2;
            {var subQ0=sQuery(id+"F0.wireOp",EDGE,"E55");Q2=makeQuery(id+"F0.imprint","IMPRINT",FACE,{"disambiguationData":[TD([[makeQuery(id+"F0.imprint","IMPRINT",EDGE,{"derivedFrom":subQ0}),1.0]])]});}
            var Q3;
            {var subQ0=sQuery(id+"F0.wireOp",EDGE,"E52");Q3=makeQuery(id+"F0.imprint","IMPRINT",FACE,{"disambiguationData":[TD([[makeQuery(id+"F0.imprint","IMPRINT",EDGE,{"derivedFrom":subQ0}),1.0]])]});}
            var Q4;
            {var subQ0=sQuery(id+"F0.wireOp",EDGE,"E53");Q4=makeQuery(id+"F0.imprint","IMPRINT",FACE,{"disambiguationData":[TD([[makeQuery(id+"F0.imprint","IMPRINT",EDGE,{"derivedFrom":subQ0}),-1.0]])]});}
            extrude(context, id + "F3", {"entities" : qUnion([Q0, Q1, Q2, Q3, Q4]), "endBound" : BoundingType.SYMMETRIC, "depth" : 3.05 * mm, "offsetDistance" : 25.4 * mm});
        }
        {
            var Q0;
            {var subQ0=sQuery(id+"F0.wireOp",EDGE,"E59");var subQ1=sQuery(id+"F0.wireOp",EDGE,"E48");var subQ2=makeQuery(id+"F0.imprint","INTERSECT",VERTEX,{"derivedFrom":[subQ1,subQ0]});Q0=makeQuery(id+"F0.imprint","IMPRINT",FACE,{"disambiguationData":[TD([[makeQuery(id+"F0.imprint","IMPRINT",EDGE,{"disambiguationData":[TD([[subQ2,-1.0]])],"derivedFrom":subQ1}),1.0]])]});}
            var Q1;
            {var subQ0=sQuery(id+"F0.wireOp",EDGE,"E58");Q1=makeQuery(id+"F0.imprint","IMPRINT",FACE,{"disambiguationData":[TD([[makeQuery(id+"F0.imprint","IMPRINT",EDGE,{"derivedFrom":subQ0}),1.0]])]});}
            var Q2;
            {var subQ0=sQuery(id+"F0.wireOp",EDGE,"E59");var subQ1=sQuery(id+"F0.wireOp",EDGE,"E48");var subQ2=makeQuery(id+"F0.imprint","INTERSECT",VERTEX,{"derivedFrom":[subQ1,subQ0]});Q2=makeQuery(id+"F0.imprint","IMPRINT",FACE,{"disambiguationData":[TD([[makeQuery(id+"F0.imprint","IMPRINT",EDGE,{"disambiguationData":[TD([[subQ2,-1.0]])],"derivedFrom":subQ1}),-1.0]])]});}
            var Q3;
            {var subQ0=sQuery(id+"F0.wireOp",EDGE,"E61");var subQ1=sQuery(id+"F0.wireOp",EDGE,"E51");var subQ2=makeQuery(id+"F0.imprint","INTERSECT",VERTEX,{"derivedFrom":[subQ1,subQ0]});Q3=makeQuery(id+"F0.imprint","IMPRINT",FACE,{"disambiguationData":[TD([[makeQuery(id+"F0.imprint","IMPRINT",EDGE,{"disambiguationData":[TD([[subQ2,-1.0]])],"derivedFrom":subQ1}),1.0]])]});}
            var Q4;
            {var subQ0=sQuery(id+"F0.wireOp",EDGE,"E56");var subQ1=makeQuery(id+"F0.imprint","INTERSECT",VERTEX,{"derivedFrom":[subQ0,sQuery(id+"F0.wireOp",EDGE,"E59")]});Q4=makeQuery(id+"F0.imprint","IMPRINT",FACE,{"disambiguationData":[TD([[makeQuery(id+"F0.imprint","IMPRINT",EDGE,{"disambiguationData":[TD([[subQ1,1.0]])],"derivedFrom":subQ0}),1.0]])]});}
            var Q5;
            {var subQ0=sQuery(id+"F0.wireOp",EDGE,"E65");var subQ1=sQuery(id+"F0.wireOp",EDGE,"E44");var subQ2=makeQuery(id+"F0.imprint","INTERSECT",VERTEX,{"derivedFrom":[subQ1,subQ0]});Q5=makeQuery(id+"F0.imprint","IMPRINT",FACE,{"disambiguationData":[TD([[makeQuery(id+"F0.imprint","IMPRINT",EDGE,{"disambiguationData":[TD([[subQ2,-1.0]])],"derivedFrom":subQ1}),-1.0]])]});}
            var Q6;
            {var subQ0=sQuery(id+"F0.wireOp",EDGE,"E63");var subQ1=sQuery(id+"F0.wireOp",EDGE,"E51");var subQ2=makeQuery(id+"F0.imprint","INTERSECT",VERTEX,{"derivedFrom":[subQ1,subQ0]});Q6=makeQuery(id+"F0.imprint","IMPRINT",FACE,{"disambiguationData":[TD([[makeQuery(id+"F0.imprint","IMPRINT",EDGE,{"disambiguationData":[TD([[subQ2,-1.0]])],"derivedFrom":subQ1}),1.0]])]});}
            var Q7;
            {var subQ0=sQuery(id+"F0.wireOp",EDGE,"E63");var subQ1=sQuery(id+"F0.wireOp",EDGE,"E45");var subQ2=makeQuery(id+"F0.imprint","INTERSECT",VERTEX,{"derivedFrom":[subQ1,subQ0]});Q7=makeQuery(id+"F0.imprint","IMPRINT",FACE,{"disambiguationData":[TD([[makeQuery(id+"F0.imprint","IMPRINT",EDGE,{"disambiguationData":[TD([[subQ2,1.0]])],"derivedFrom":subQ1}),1.0]])]});}
            var Q8;
            {var subQ0=sQuery(id+"F0.wireOp",EDGE,"E65");var subQ1=sQuery(id+"F0.wireOp",EDGE,"E44");var subQ2=makeQuery(id+"F0.imprint","INTERSECT",VERTEX,{"derivedFrom":[subQ1,subQ0]});Q8=makeQuery(id+"F0.imprint","IMPRINT",FACE,{"disambiguationData":[TD([[makeQuery(id+"F0.imprint","IMPRINT",EDGE,{"disambiguationData":[TD([[subQ2,-1.0]])],"derivedFrom":subQ1}),1.0]])]});}
            var Q9;
            {var subQ0=sQuery(id+"F0.wireOp",EDGE,"E62");Q9=makeQuery(id+"F0.imprint","IMPRINT",FACE,{"disambiguationData":[TD([[makeQuery(id+"F0.imprint","IMPRINT",EDGE,{"derivedFrom":subQ0}),-1.0]])]});}
            extrude(context, id + "F4", {"entities" : qUnion([Q0, Q1, Q2, Q3, Q4, Q5, Q6, Q7, Q8, Q9]), "endBound" : BoundingType.SYMMETRIC, "depth" : 5.08 * mm, "offsetDistance" : 25.4 * mm});
        }
        {
            var Q0;
            {var subQ0=sQuery(id+"F0.wireOp",EDGE,"E9");Q0=makeQuery(id+"F0.imprint","IMPRINT",FACE,{"disambiguationData":[TD([[makeQuery(id+"F0.imprint","IMPRINT",EDGE,{"derivedFrom":subQ0}),-1.0]])]});}
            var Q1;
            {var subQ8=sQuery(id+"F0.wireOp",EDGE,"E10");Q1=makeQuery(id+"F0.imprint","IMPRINT",FACE,{"disambiguationData":[TD([[makeQuery(id+"F0.imprint","IMPRINT",EDGE,{"derivedFrom":subQ8}),-1.0]])]});}
            var Q2;
            {var subQ0=sQuery(id+"F0.wireOp",EDGE,"E62");Q2=makeQuery(id+"F0.imprint","IMPRINT",FACE,{"disambiguationData":[TD([[makeQuery(id+"F0.imprint","IMPRINT",EDGE,{"derivedFrom":subQ0}),1.0]])]});}
            extrude(context, id + "F5", {"entities" : qUnion([Q0, Q1, Q2]), "endBound" : BoundingType.SYMMETRIC, "depth" : 5.84 * mm, "offsetDistance" : 25.4 * mm});
        }
        {
            var Q0;
            {var subQ0=sQuery(id+"F0.wireOp",EDGE,"E63");var subQ1=sQuery(id+"F0.wireOp",EDGE,"E45");var subQ2=makeQuery(id+"F0.imprint","INTERSECT",VERTEX,{"derivedFrom":[subQ1,subQ0]});Q0=makeQuery(id+"F0.imprint","IMPRINT",FACE,{"disambiguationData":[TD([[makeQuery(id+"F0.imprint","IMPRINT",EDGE,{"disambiguationData":[TD([[subQ2,-1.0]])],"derivedFrom":subQ1}),1.0]])]});}
            var Q1;
            {var subQ4=sQuery(id+"F0.wireOp",EDGE,"E12");Q1=makeQuery(id+"F0.imprint","IMPRINT",FACE,{"disambiguationData":[TD([[makeQuery(id+"F0.imprint","IMPRINT",EDGE,{"derivedFrom":subQ4}),-1.0]])]});}
            var Q2;
            {var subQ0=sQuery(id+"F0.wireOp",EDGE,"E49");Q2=makeQuery(id+"F0.imprint","IMPRINT",FACE,{"disambiguationData":[TD([[makeQuery(id+"F0.imprint","IMPRINT",EDGE,{"derivedFrom":subQ0}),1.0]])]});}
            extrude(context, id + "F6", {"entities" : qUnion([Q0, Q1, Q2]), "endBound" : BoundingType.SYMMETRIC, "depth" : 1.12 * mm, "offsetDistance" : 25.4 * mm});
        }
    });
